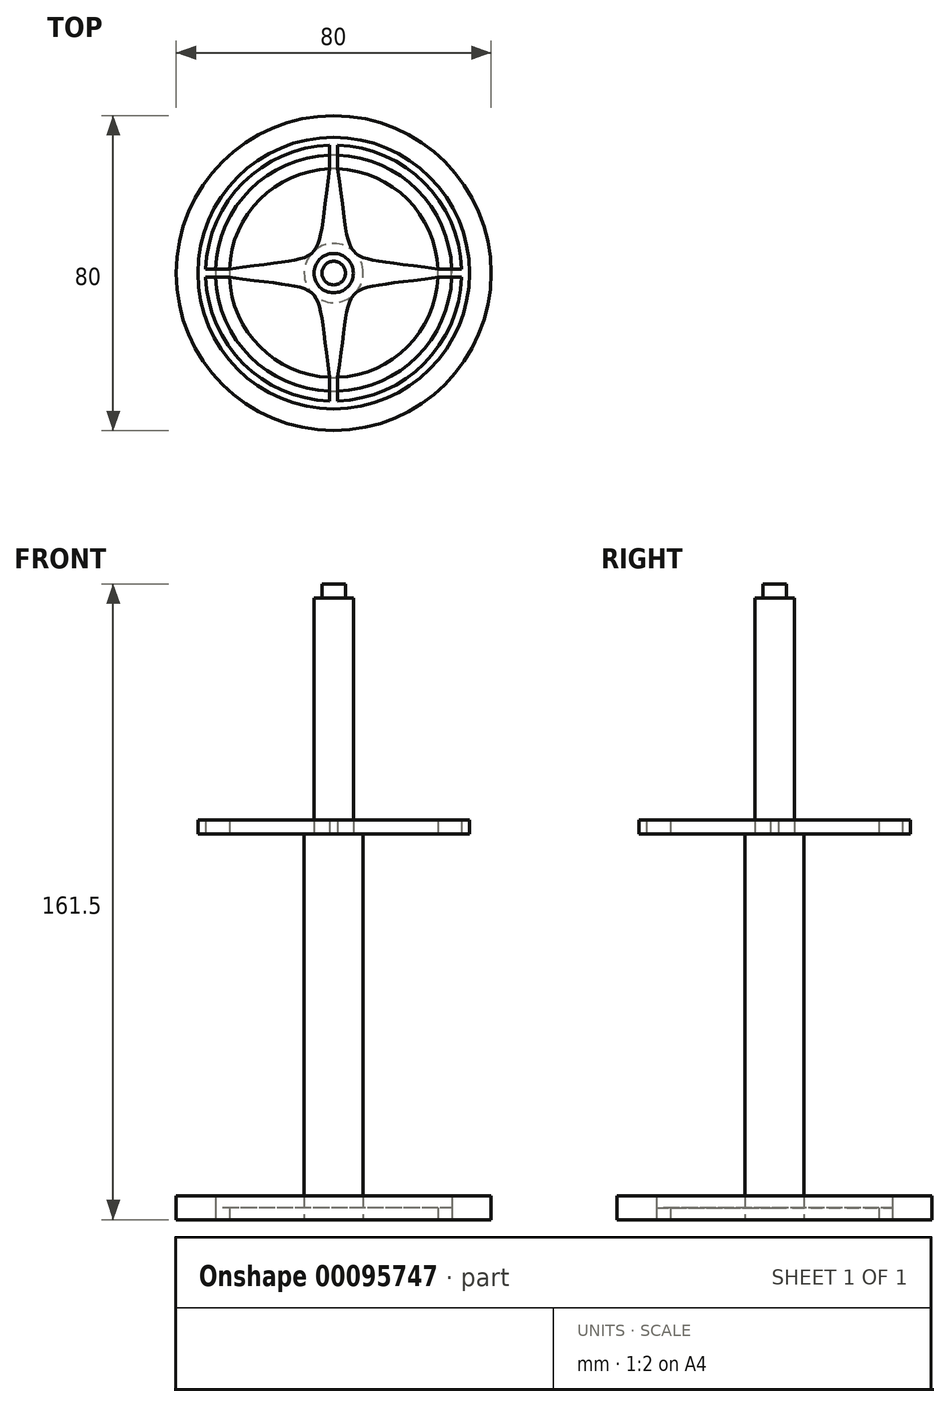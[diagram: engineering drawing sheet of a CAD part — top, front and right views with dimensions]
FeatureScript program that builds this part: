
annotation { "Feature Type Name" : "Feature", "Feature Type Description" : "" }
export const myFeature = defineFeature(function(context is Context, id is Id, definition is map)
    precondition{}
    {
        {
            var Q0;
            Q0=qCreatedBy(makeId("Top.planeOp"),FACE);
            var sketch = newSketch(context, id + "F0", { "sketchPlane" : qUnion([Q0])});
            skCircle(sketch, "E0", {"center": v(0, 0) * mm, "radius": 40 * mm});
            skCircle(sketch, "E1", {"center": v(0, 0) * mm, "radius": 30 * mm});
            skCircle(sketch, "E2", {"center": v(0, 0) * mm, "radius": 26.5 * mm});
            skCircle(sketch, "E3", {"center": v(0, 0) * mm, "radius": 7.5 * mm});
            skSolve(sketch);
        }
        {
            var Q0;
            Q0=makeQuery(id+"F0.imprint","IMPRINT",FACE,{"disambiguationData":[TD([[makeQuery(id+"F0.imprint","IMPRINT",EDGE,{"derivedFrom":sQuery(id+"F0.wireOp",EDGE,"E3")}),1.0]])]});
            var Q1;
            Q1=makeQuery(id+"F0.imprint","IMPRINT",FACE,{"disambiguationData":[TD([[makeQuery(id+"F0.imprint","IMPRINT",EDGE,{"derivedFrom":sQuery(id+"F0.wireOp",EDGE,"E0")}),1.0]])]});
            var Q2;
            {var subQ0=sQuery(id+"F0.wireOp",EDGE,"bb9416e4-7aad-4895-abd7-882a3f8e9b0e");Q2=makeQuery(id+"F0.imprint","IMPRINT",FACE,{"disambiguationData":[TD([[makeQuery(id+"F0.imprint","IMPRINT",EDGE,{"derivedFrom":subQ0}),1.0]])]});}
            var Q3;
            {var subQ0=sQuery(id+"F0.wireOp",EDGE,"dcbf5964-eba2-468b-b0c6-7a0db69ada310.MirrorCS");Q3=makeQuery(id+"F0.imprint","IMPRINT",FACE,{"disambiguationData":[TD([[makeQuery(id+"F0.imprint","IMPRINT",EDGE,{"derivedFrom":subQ0}),-1.0]])]});}
            var Q4;
            {var subQ0=sQuery(id+"F0.wireOp",EDGE,"f122a61b-da9a-4869-974b-a36e2a6797fb0.MirrorCS");Q4=makeQuery(id+"F0.imprint","IMPRINT",FACE,{"disambiguationData":[TD([[makeQuery(id+"F0.imprint","IMPRINT",EDGE,{"derivedFrom":subQ0}),1.0]])]});}
            var Q5;
            {var subQ0=sQuery(id+"F0.wireOp",EDGE,"b1b10cdf-783c-4f86-9f8d-ae239cad31dc0.MirrorCS");Q5=makeQuery(id+"F0.imprint","IMPRINT",FACE,{"disambiguationData":[TD([[makeQuery(id+"F0.imprint","IMPRINT",EDGE,{"derivedFrom":subQ0}),-1.0]])]});}
            extrude(context, id + "F1", {"entities" : qUnion([Q0, Q1, Q2, Q3, Q4, Q5]), "depth" : 6 * mm});
        }
        {
            var Q0;
            Q0=makeQuery(id+"F0.imprint","IMPRINT",FACE,{"disambiguationData":[TD([[makeQuery(id+"F0.imprint","IMPRINT",EDGE,{"derivedFrom":sQuery(id+"F0.wireOp",EDGE,"E1")}),1.0]])]});
            extrude(context, id + "F2", {"entities" : qUnion([Q0]), "depth" : 3 * mm});
        }
        {
            var Q0;
            Q0=makeQuery(id+"F0.imprint","IMPRINT",FACE,{"disambiguationData":[TD([[makeQuery(id+"F0.imprint","IMPRINT",EDGE,{"derivedFrom":sQuery(id+"F0.wireOp",EDGE,"E3")}),1.0]])]});
            extrude(context, id + "F3", {"entities" : qUnion([Q0]), "operationType" : NewBodyOperationType.ADD, "depth" : 98 * mm});
        }
        {
            var Q0;
            Q0=makeQuery(id+"F3.opExtrude","CAP_FACE",FACE,{"disambiguationData":[OSD([sQuery(id+"F0.wireOp",EDGE,"E3")])],"isStart":false});
            var sketch = newSketch(context, id + "F4", { "sketchPlane" : qUnion([Q0])});
            skCircle(sketch, "E4", {"center": v(0, 0) * mm, "radius": 5 * mm});
            skCircle(sketch, "E5.0", {"center": v(0, 0) * mm, "radius": 7.5 * mm});
            skSolve(sketch);
        }
        {
            var Q0;
            Q0=makeQuery(id+"F4.imprint","IMPRINT",FACE,{"disambiguationData":[TD([[makeQuery(id+"F4.imprint","IMPRINT",EDGE,{"derivedFrom":sQuery(id+"F4.wireOp",EDGE,"E4")}),1.0]])]});
            extrude(context, id + "F5", {"entities" : qUnion([Q0]), "operationType" : NewBodyOperationType.ADD, "depth" : 60 * mm});
        }
        {
            var Q0;
            Q0=makeQuery(id+"F5.opExtrude","CAP_FACE",FACE,{"disambiguationData":[OSD([sQuery(id+"F4.wireOp",EDGE,"E4")])],"isStart":false});
            var sketch = newSketch(context, id + "F6", { "sketchPlane" : qUnion([Q0])});
            skCircle(sketch, "E6", {"center": v(0, 0) * mm, "radius": 3 * mm});
            skCircle(sketch, "E7.0", {"center": v(0, 0) * mm, "radius": 5 * mm});
            skSolve(sketch);
        }
        {
            var Q0;
            Q0=makeQuery(id+"F6.imprint","IMPRINT",FACE,{"disambiguationData":[TD([[makeQuery(id+"F6.imprint","IMPRINT",EDGE,{"derivedFrom":sQuery(id+"F6.wireOp",EDGE,"E6")}),1.0]])]});
            extrude(context, id + "F7", {"entities" : qUnion([Q0]), "operationType" : NewBodyOperationType.ADD, "depth" : 3.5 * mm});
        }
        {
            var Q0;
            Q0=makeQuery(id+"F3.opExtrude","CAP_FACE",FACE,{"disambiguationData":[OSD([sQuery(id+"F0.wireOp",EDGE,"E3")])],"isStart":false});
            var sketch = newSketch(context, id + "F8", { "sketchPlane" : qUnion([Q0])});
            skArc(sketch, "E8.0", {"start": v(-26.48, -1) * mm, "mid": v(-18.74, -18.74) * mm, "end": v(-1, -26.48) * mm});
            skArc(sketch, "E9", {"start": v(-1, 32.48) * mm, "mid": v(-22.98, 22.98) * mm, "end": v(-32.48, 1) * mm});
            skLineSegment(sketch, "E10", {"start": v(0, 32.5) * mm, "end": v(0, 0) * mm});
            skLineSegment(sketch, "E11", {"start": v(32.5, 0) * mm, "end": v(-32.5, 0) * mm, "construction": true});
            skLineSegment(sketch, "E12", {"start": v(0, 0) * mm, "end": v(0, -32.5) * mm, "construction": true});
            skLineSegment(sketch, "E13", {"start": v(1, 32.48) * mm, "end": v(1, 26.48) * mm});
            skLineSegment(sketch, "E14.MirrorCS", {"start": v(-1, 32.48) * mm, "end": v(-1, 26.48) * mm});
            skLineSegment(sketch, "E15.MirrorCS", {"start": v(1, -32.48) * mm, "end": v(1, -26.48) * mm});
            skLineSegment(sketch, "E16.MirrorCS", {"start": v(-1, -32.48) * mm, "end": v(-1, -26.48) * mm});
            skLineSegment(sketch, "E17", {"start": v(-32.48, 1) * mm, "end": v(-26.48, 1) * mm});
            skLineSegment(sketch, "E18.MirrorCS", {"start": v(-32.48, -1) * mm, "end": v(-26.48, -1) * mm});
            skLineSegment(sketch, "E19.MirrorCS", {"start": v(32.48, 1) * mm, "end": v(26.48, 1) * mm});
            skLineSegment(sketch, "E20.MirrorCS", {"start": v(32.48, -1) * mm, "end": v(26.48, -1) * mm});
            skArc(sketch, "E21.trimOffspring", {"start": v(1, -26.48) * mm, "mid": v(18.74, -18.74) * mm, "end": v(26.48, -1) * mm});
            skArc(sketch, "E22.trimOffspring", {"start": v(26.48, 1) * mm, "mid": v(0, 26.5) * mm, "end": v(-26.48, 1) * mm});
            skArc(sketch, "E23.trimOffspring", {"start": v(-32.48, -1) * mm, "mid": v(-22.98, -22.98) * mm, "end": v(-1, -32.48) * mm});
            skArc(sketch, "E24.trimOffspring", {"start": v(1, -32.48) * mm, "mid": v(22.98, -22.98) * mm, "end": v(32.48, -1) * mm});
            skArc(sketch, "E25.trimOffspring", {"start": v(32.48, 1) * mm, "mid": v(22.98, 22.98) * mm, "end": v(1, 32.48) * mm});
            skCircle(sketch, "E26", {"center": v(0, 0) * mm, "radius": 34.5 * mm});
            skCircle(sketch, "E27.0", {"center": v(0, 0) * mm, "radius": 5 * mm});
            skFitSpline(sketch, "E28", {"points": [v(1, 26.48) * mm, v(26.48, 1) * mm], "startDerivative": vector(12, -79.44) * mm, "endDerivative": vector(79.44, -12) * mm});
            skFitSpline(sketch, "E29.MirrorCS", {"points": [v(1, -26.48) * mm, v(26.48, -1) * mm], "startDerivative": vector(12, 79.44) * mm, "endDerivative": vector(79.44, 12) * mm});
            skFitSpline(sketch, "E30.MirrorCS", {"points": [v(1, -26.48) * mm, v(26.48, -1) * mm], "startDerivative": vector(12, 79.44) * mm, "endDerivative": vector(79.44, 12) * mm});
            skFitSpline(sketch, "E31.MirrorCS", {"points": [v(-1, 26.48) * mm, v(-26.48, 1) * mm], "startDerivative": vector(-12, -79.44) * mm, "endDerivative": vector(-79.44, -12) * mm});
            skFitSpline(sketch, "E32.MirrorCS", {"points": [v(-1, -26.48) * mm, v(-26.48, -1) * mm], "startDerivative": vector(-12, 79.44) * mm, "endDerivative": vector(-79.44, 12) * mm});
            skPoint(sketch, "E33.end.orphan", {"position": v(-7.43, 1) * mm});
            skPoint(sketch, "E34.MirrorCS.end.orphan", {"position": v(-7.43, -1) * mm});
            skPoint(sketch, "E35.end.orphan", {"position": v(-1, 7.43) * mm});
            skPoint(sketch, "E36.MirrorCS.end.orphan", {"position": v(1, 7.43) * mm});
            skPoint(sketch, "E37.MirrorCS.end.orphan", {"position": v(7.43, 1) * mm});
            skPoint(sketch, "E38.MirrorCS.end.orphan", {"position": v(7.43, -1) * mm});
            skPoint(sketch, "E39.MirrorCS.end.orphan", {"position": v(1, -7.43) * mm});
            skPoint(sketch, "E40.MirrorCS.end.orphan", {"position": v(-1, -7.43) * mm});
            skSolve(sketch);
        }
        {
            var Q0;
            Q0=makeQuery(id+"F8.imprint","IMPRINT",FACE,{"disambiguationData":[TD([[makeQuery(id+"F8.imprint","IMPRINT",EDGE,{"derivedFrom":sQuery(id+"F8.wireOp",EDGE,"E27.0")}),-1.0]])]});
            var Q1;
            Q1=makeQuery(id+"F8.imprint","IMPRINT",FACE,{"disambiguationData":[TD([[makeQuery(id+"F8.imprint","IMPRINT",EDGE,{"derivedFrom":sQuery(id+"F8.wireOp",EDGE,"E9")}),-1.0]])]});
            var Q2;
            {var subQ2=sQuery(id+"F8.wireOp",EDGE,"E35");Q2=makeQuery(id+"F8.imprint","IMPRINT",FACE,{"disambiguationData":[TD([[makeQuery(id+"F8.imprint","IMPRINT",EDGE,{"derivedFrom":subQ2}),1.0]])]});}
            extrude(context, id + "F9", {"entities" : qUnion([Q0, Q1, Q2]), "depth" : 3.5 * mm});
        }
    });
